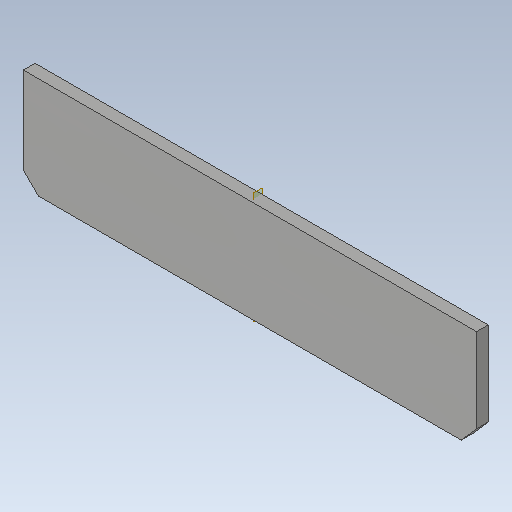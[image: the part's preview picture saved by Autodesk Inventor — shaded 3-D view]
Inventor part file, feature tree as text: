
AUTODESK INVENTOR PART (.ipt)
format: ipt  version: 2020.1 (Build 241239000, 239)  size: 137,728 bytes
history: native  units: mm
features: other x6, plane x1, sheet_metal_op x1, sketch x1, reference x1
ambient origin geometry x8: Origin, YZ Plane, XZ Plane, XY Plane, X Axis, Y Axis, Z Axis, Center Point
bodies: Solid1 (feature_tree)
feature tree (10):
  plane  "Work Plane1"
  sheet_metal_op  "Face1"
  other  "midtplan"
  sketch  "Sketch1"  dims[d3=45.0deg d4=7.171149mm d5=30.0mm d6=2.0mm d7=3.0mm]
  reference  "Reference1"
  other  "Plate1"
  parser-record x1  (decoder bookkeeping rows leaked as tree rows — omitted from the tree; the rows remain in map.json)
  other  "modul.iam"
  other  "plade:1"
  other  "Definition1"
note: 1 file-system path scrubbed to <path> (originals preserved in map.json)
